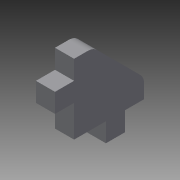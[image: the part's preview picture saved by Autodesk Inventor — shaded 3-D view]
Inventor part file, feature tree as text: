
AUTODESK INVENTOR PART (.ipt)
format: ipt  version: 2015 (Build 190159000, 159)  size: 90,624 bytes
history: native  units: mm
features: extrude x1, sketch x1
ambient origin geometry x8: Origin, YZ Plane, XZ Plane, XY Plane, X Axis, Y Axis, Z Axis, Center Point
bodies: Solid1 (feature_tree)
feature tree (2):
  extrude  "Extrusion1"  Depth=3.0mm
  sketch  "Sketch1"  dims[d0=5.0mm d1=3.0mm d2=3.0mm d3=5.0mm d4=3.0mm d5=3.0mm d6=3.0mm d7=3.0mm d8=3.0mm d9=3.0mm d10=3.0mm d11=3.0mm d12=3.0mm d13=0.0mm d14=2.0mm]
